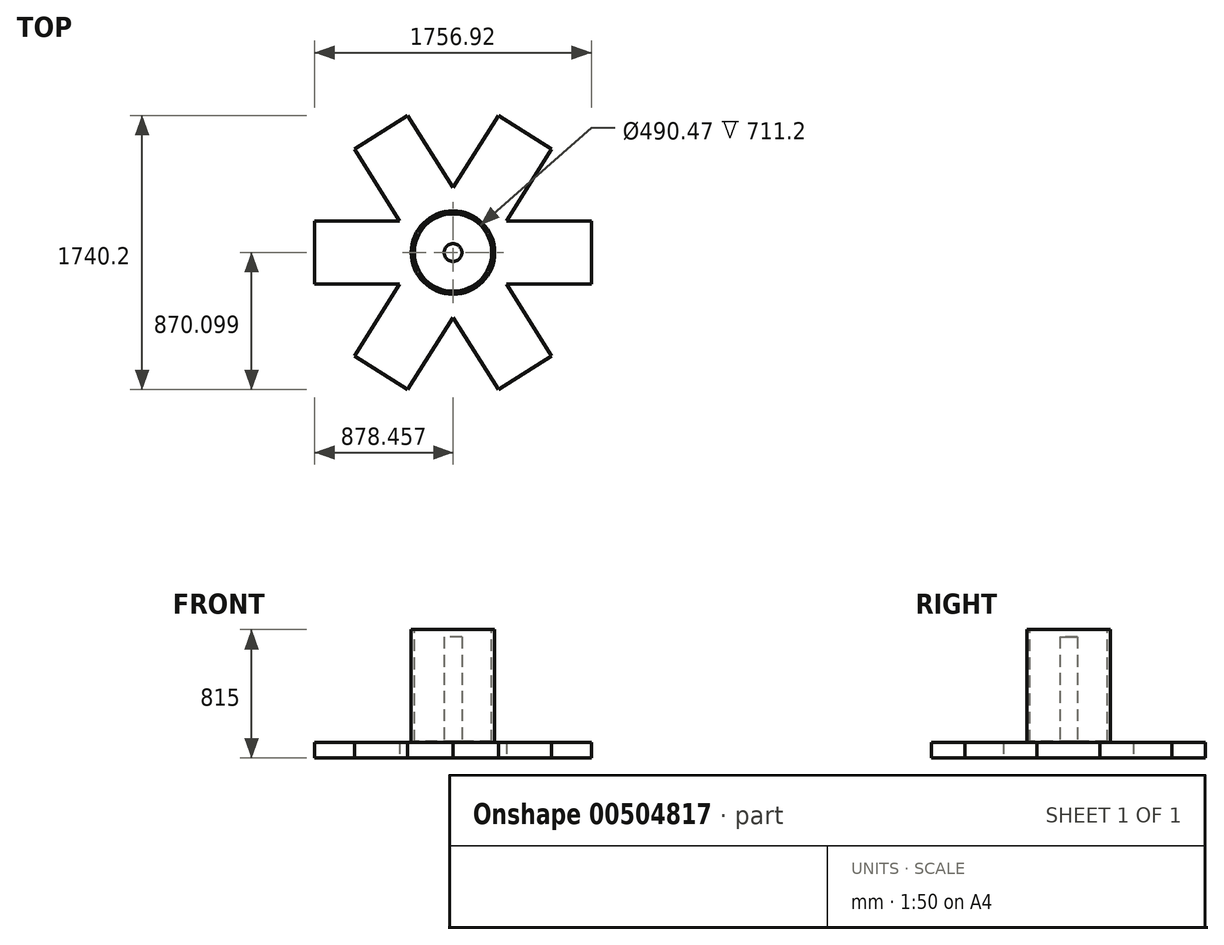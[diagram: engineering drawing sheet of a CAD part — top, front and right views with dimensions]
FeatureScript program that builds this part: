
annotation { "Feature Type Name" : "Feature", "Feature Type Description" : "" }
export const myFeature = defineFeature(function(context is Context, id is Id, definition is map)
    precondition{}
    {
        {
            var Q0;
            Q0=qCreatedBy(makeId("Top.planeOp"),FACE);
            var sketch = newSketch(context, id + "F0", { "sketchPlane" : qUnion([Q0])});
            skLineSegment(sketch, "E0", {"start": v(124.65, 246.73) * mm, "end": v(124.65, -153.27) * mm});
            skLineSegment(sketch, "E1", {"start": v(124.65, 246.73) * mm, "end": v(-213.81, 459.9) * mm});
            skLineSegment(sketch, "E2", {"start": v(-213.81, 459.9) * mm, "end": v(-552.27, 246.73) * mm});
            skLineSegment(sketch, "E3", {"start": v(-552.27, 246.73) * mm, "end": v(-552.27, -153.27) * mm});
            skLineSegment(sketch, "E4", {"start": v(-213.81, -366.45) * mm, "end": v(-552.27, -153.27) * mm});
            skLineSegment(sketch, "E5", {"start": v(-213.81, -366.45) * mm, "end": v(124.65, -153.27) * mm});
            skSolve(sketch);
        }
        {
            var Q0;
            Q0=makeQuery(id+"F0.imprint","IMPRINT",FACE,{"disambiguationData":[TD([[makeQuery(id+"F0.imprint","IMPRINT",EDGE,{"derivedFrom":sQuery(id+"F0.wireOp",EDGE,"E0")}),-1.0]])]});
            extrude(context, id + "F1", {"entities" : qUnion([Q0]), "depth" : 100 * mm});
        }
        {
            var Q0;
            Q0=makeQuery(id+"F1.opExtrude","CAP_FACE",FACE,{"disambiguationData":[OSD([sQuery(id+"F0.wireOp",EDGE,"E0"),sQuery(id+"F0.wireOp",EDGE,"E1"),sQuery(id+"F0.wireOp",EDGE,"E2"),sQuery(id+"F0.wireOp",EDGE,"E3"),sQuery(id+"F0.wireOp",EDGE,"E4"),sQuery(id+"F0.wireOp",EDGE,"E5")])],"isStart":false});
            var sketch = newSketch(context, id + "F2", { "sketchPlane" : qUnion([Q0])});
            skCircle(sketch, "E6", {"center": v(-213.81, 46.73) * mm, "radius": 265.19 * mm});
            skPoint(sketch, "E6.centerSnap0", {"position": v(124.65, 46.73) * mm});
            skSolve(sketch);
        }
        {
            var Q0;
            Q0=makeQuery(id+"F2.imprint","IMPRINT",FACE,{"disambiguationData":[TD([[makeQuery(id+"F2.imprint","IMPRINT",EDGE,{"derivedFrom":sQuery(id+"F2.wireOp",EDGE,"E6")}),1.0]])]});
            var Q1;
            Q1=sQuery(id+"F2.wireOp",EDGE,"E6");
            extrude(context, id + "F3", {"entities" : qUnion([Q0]), "surfaceEntities" : qUnion([Q1]), "depth" : 715 * mm, "offsetDistance" : 25.4 * mm});
        }
        {
            var Q0;
            Q0=makeQuery(id+"F1.opExtrude","SWEPT_FACE",FACE,{"disambiguationData":[OSD([sQuery(id+"F0.wireOp",EDGE,"E5")])]});
            extrude(context, id + "F4", {"entities" : qUnion([Q0]), "operationType" : NewBodyOperationType.ADD, "depth" : 540 * mm});
        }
        {
            var Q0;
            Q0=makeQuery(id+"F1.opExtrude","SWEPT_FACE",FACE,{"disambiguationData":[OSD([sQuery(id+"F0.wireOp",EDGE,"E0")])]});
            extrude(context, id + "F5", {"entities" : qUnion([Q0]), "operationType" : NewBodyOperationType.ADD, "depth" : 540 * mm});
        }
        {
            var Q0;
            Q0=makeQuery(id+"F1.opExtrude","SWEPT_FACE",FACE,{"disambiguationData":[OSD([sQuery(id+"F0.wireOp",EDGE,"E4")])]});
            extrude(context, id + "F6", {"entities" : qUnion([Q0]), "operationType" : NewBodyOperationType.ADD, "depth" : 540 * mm});
        }
        {
            var Q0;
            Q0=makeQuery(id+"F1.opExtrude","SWEPT_FACE",FACE,{"disambiguationData":[OSD([sQuery(id+"F0.wireOp",EDGE,"E3")])]});
            extrude(context, id + "F7", {"entities" : qUnion([Q0]), "operationType" : NewBodyOperationType.ADD, "depth" : 540 * mm});
        }
        {
            var Q0;
            Q0=makeQuery(id+"F1.opExtrude","SWEPT_FACE",FACE,{"disambiguationData":[OSD([sQuery(id+"F0.wireOp",EDGE,"E2")])]});
            extrude(context, id + "F8", {"entities" : qUnion([Q0]), "operationType" : NewBodyOperationType.ADD, "depth" : 540 * mm});
        }
        {
            var Q0;
            Q0=makeQuery(id+"F1.opExtrude","SWEPT_FACE",FACE,{"disambiguationData":[OSD([sQuery(id+"F0.wireOp",EDGE,"E1")])]});
            extrude(context, id + "F9", {"entities" : qUnion([Q0]), "operationType" : NewBodyOperationType.ADD, "depth" : 540 * mm});
        }
        {
            var Q0;
            Q0=makeQuery(id+"F3.opExtrude","CAP_FACE",FACE,{"disambiguationData":[OSD([sQuery(id+"F2.wireOp",EDGE,"E6")])],"isStart":false});
            var sketch = newSketch(context, id + "F10", { "sketchPlane" : qUnion([Q0])});
            skCircle(sketch, "E7", {"center": v(-213.81, 46.73) * mm, "radius": 245.24 * mm});
            skSolve(sketch);
        }
        {
            var Q0;
            Q0=makeQuery(id+"F10.imprint","IMPRINT",FACE,{"disambiguationData":[TD([[makeQuery(id+"F10.imprint","IMPRINT",EDGE,{"derivedFrom":sQuery(id+"F10.wireOp",EDGE,"E7")}),1.0]])]});
            var Q1;
            Q1=sQuery(id+"F10.wireOp",EDGE,"E7");
            extrude(context, id + "F11", {"entities" : qUnion([Q0]), "operationType" : NewBodyOperationType.REMOVE, "surfaceEntities" : qUnion([Q1]), "oppositeDirection" : true, "depth" : 711.2 * mm, "offsetDistance" : 25.4 * mm});
        }
        {
            var Q0;
            Q0=makeQuery(id+"F11.boolean.opBoolean","COPY",FACE,{"derivedFrom":makeQuery(id+"F11.opExtrude","CAP_FACE",FACE,{"disambiguationData":[OSD([sQuery(id+"F10.wireOp",EDGE,"E7")])],"isStart":false})});
            var sketch = newSketch(context, id + "F12", { "sketchPlane" : qUnion([Q0])});
            skCircle(sketch, "E8", {"center": v(-213.81, 46.73) * mm, "radius": 56.2 * mm});
            skSolve(sketch);
        }
        {
            var Q0;
            Q0=makeQuery(id+"F12.imprint","IMPRINT",FACE,{"disambiguationData":[TD([[makeQuery(id+"F12.imprint","IMPRINT",EDGE,{"derivedFrom":sQuery(id+"F12.wireOp",EDGE,"E8")}),1.0]])]});
            var Q1;
            Q1=sQuery(id+"F12.wireOp",EDGE,"E8");
            extrude(context, id + "F13", {"entities" : qUnion([Q0]), "operationType" : NewBodyOperationType.ADD, "surfaceEntities" : qUnion([Q1]), "depth" : 665.48 * mm, "offsetDistance" : 25.4 * mm});
        }
    });
